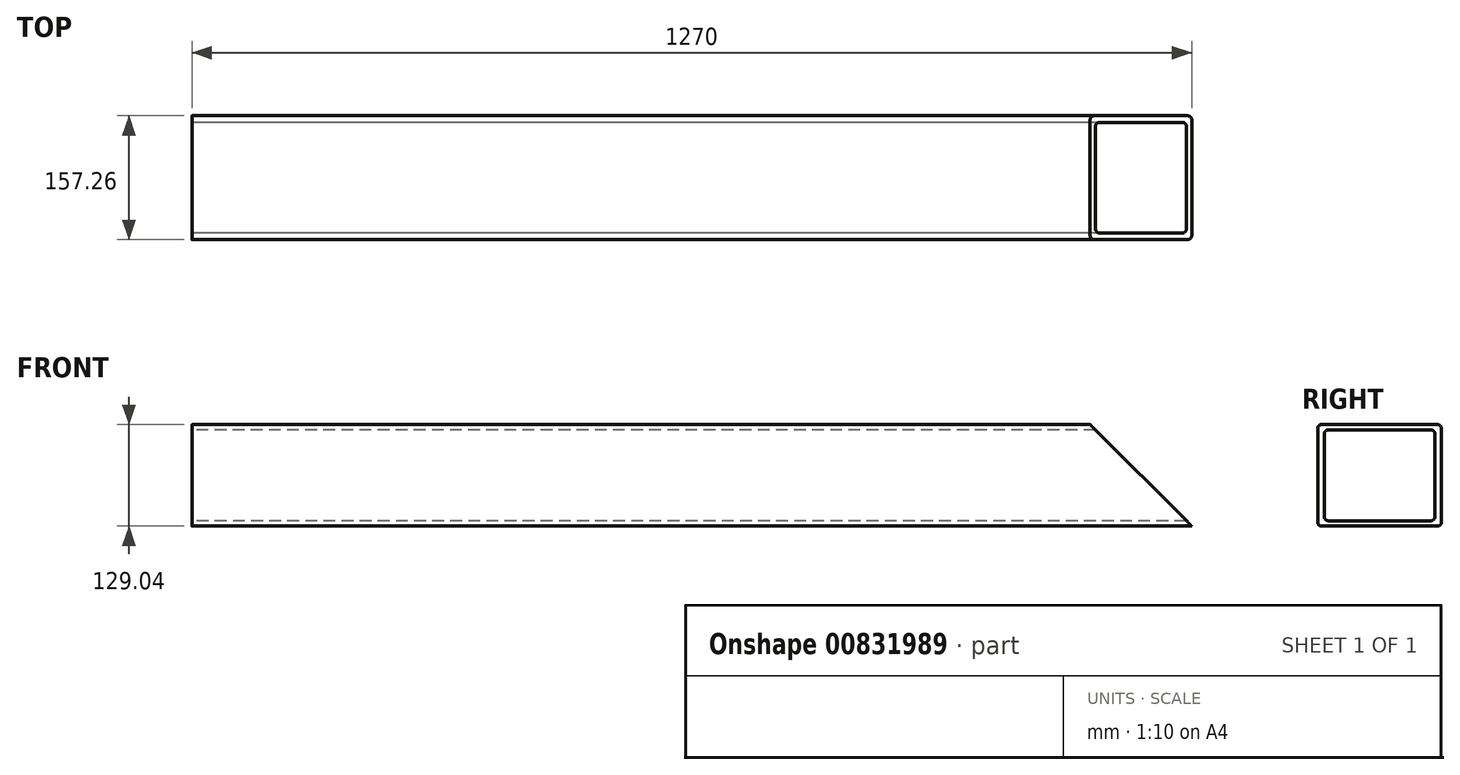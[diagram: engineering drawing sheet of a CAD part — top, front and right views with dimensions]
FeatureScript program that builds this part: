
annotation { "Feature Type Name" : "Feature", "Feature Type Description" : "" }
export const myFeature = defineFeature(function(context is Context, id is Id, definition is map)
    precondition{}
    {
        {
            var Q0;
            Q0=qCreatedBy(makeId("Right.planeOp"),FACE);
            var sketch = newSketch(context, id + "F0", { "sketchPlane" : qUnion([Q0])});
            skLineSegment(sketch, "E0.bottom", {"start": v(78.63, 64.52) * mm, "end": v(-78.63, 64.52) * mm});
            skLineSegment(sketch, "E0.top", {"start": v(78.63, -64.52) * mm, "end": v(-78.63, -64.52) * mm});
            skLineSegment(sketch, "E0.left", {"start": v(78.63, 64.52) * mm, "end": v(78.63, -64.52) * mm});
            skLineSegment(sketch, "E0.right", {"start": v(-78.63, 64.52) * mm, "end": v(-78.63, -64.52) * mm});
            skPoint(sketch, "E0.middle", {"position": v(0, 0) * mm});
            skLineSegment(sketch, "E1.bottom", {"start": v(70.33, 57.67) * mm, "end": v(-70.33, 57.67) * mm});
            skLineSegment(sketch, "E1.top", {"start": v(70.33, -57.67) * mm, "end": v(-70.33, -57.67) * mm});
            skLineSegment(sketch, "E1.left", {"start": v(70.33, 57.67) * mm, "end": v(70.33, -57.67) * mm});
            skLineSegment(sketch, "E1.right", {"start": v(-70.33, 57.67) * mm, "end": v(-70.33, -57.67) * mm});
            skSolve(sketch);
        }
        {
            var Q0;
            Q0 = qSketchRegion(id + "F0", true);
            extrude(context, id + "F1", {"entities" : qUnion([Q0]), "endBound" : BoundingType.SYMMETRIC, "depth" : 1270 * mm, "offsetDistance" : 25.4 * mm});
        }
        {
            var Q0;
            Q0=makeQuery(id+"F1.opExtrude","SWEPT_EDGE",EDGE,{"disambiguationData":[OSD([sQuery(id+"F0.wireOp",EDGE,"E0.bottom"),sQuery(id+"F0.wireOp",EDGE,"E0.right")])]});
            var Q1;
            Q1=makeQuery(id+"F1.opExtrude","SWEPT_EDGE",EDGE,{"disambiguationData":[OSD([sQuery(id+"F0.wireOp",EDGE,"E1.bottom"),sQuery(id+"F0.wireOp",EDGE,"E1.right")])]});
            var Q2;
            Q2=makeQuery(id+"F1.opExtrude","SWEPT_EDGE",EDGE,{"disambiguationData":[OSD([sQuery(id+"F0.wireOp",EDGE,"E1.bottom"),sQuery(id+"F0.wireOp",EDGE,"E1.left")])]});
            var Q3;
            Q3=makeQuery(id+"F1.opExtrude","SWEPT_EDGE",EDGE,{"disambiguationData":[OSD([sQuery(id+"F0.wireOp",EDGE,"E0.bottom"),sQuery(id+"F0.wireOp",EDGE,"E0.left")])]});
            var Q4;
            Q4=makeQuery(id+"F1.opExtrude","SWEPT_EDGE",EDGE,{"disambiguationData":[OSD([sQuery(id+"F0.wireOp",EDGE,"E0.top"),sQuery(id+"F0.wireOp",EDGE,"E0.left")])]});
            var Q5;
            Q5=makeQuery(id+"F1.opExtrude","SWEPT_EDGE",EDGE,{"disambiguationData":[OSD([sQuery(id+"F0.wireOp",EDGE,"E1.top"),sQuery(id+"F0.wireOp",EDGE,"E1.left")])]});
            var Q6;
            Q6=makeQuery(id+"F1.opExtrude","SWEPT_EDGE",EDGE,{"disambiguationData":[OSD([sQuery(id+"F0.wireOp",EDGE,"E1.top"),sQuery(id+"F0.wireOp",EDGE,"E1.right")])]});
            var Q7;
            Q7=makeQuery(id+"F1.opExtrude","SWEPT_EDGE",EDGE,{"disambiguationData":[OSD([sQuery(id+"F0.wireOp",EDGE,"E0.top"),sQuery(id+"F0.wireOp",EDGE,"E0.right")])]});
            fillet(context, id + "F2", {"entities" : qUnion([Q0, Q1, Q2, Q3, Q4, Q5, Q6, Q7]), "radius" : 5.08 * mm, "tangentPropagation" : true, "allowEdgeOverflow" : false});
        }
        {
            var Q0;
            Q0=makeQuery(id+"F1.opExtrude","SWEPT_FACE",FACE,{"disambiguationData":[OSD([sQuery(id+"F0.wireOp",EDGE,"E0.right")])]});
            var sketch = newSketch(context, id + "F3", { "sketchPlane" : qUnion([Q0])});
            skLineSegment(sketch, "E2", {"start": v(635, 64.52) * mm, "end": v(505.96, 64.52) * mm});
            skLineSegment(sketch, "E3", {"start": v(635, 64.52) * mm, "end": v(635, -64.52) * mm});
            skLineSegment(sketch, "E4", {"start": v(635, -64.52) * mm, "end": v(505.96, 64.52) * mm});
            skLineSegment(sketch, "E5.0", {"start": v(-635, 64.52) * mm, "end": v(635, 64.52) * mm, "construction": true});
            skSolve(sketch);
        }
        {
            var Q0;
            Q0 = qSketchRegion(id + "F3", true);
            extrude(context, id + "F4", {"entities" : qUnion([Q0]), "operationType" : NewBodyOperationType.REMOVE, "endBound" : BoundingType.THROUGH_ALL, "oppositeDirection" : true, "depth" : 25.4 * mm, "offsetDistance" : 25.4 * mm});
        }
    });
